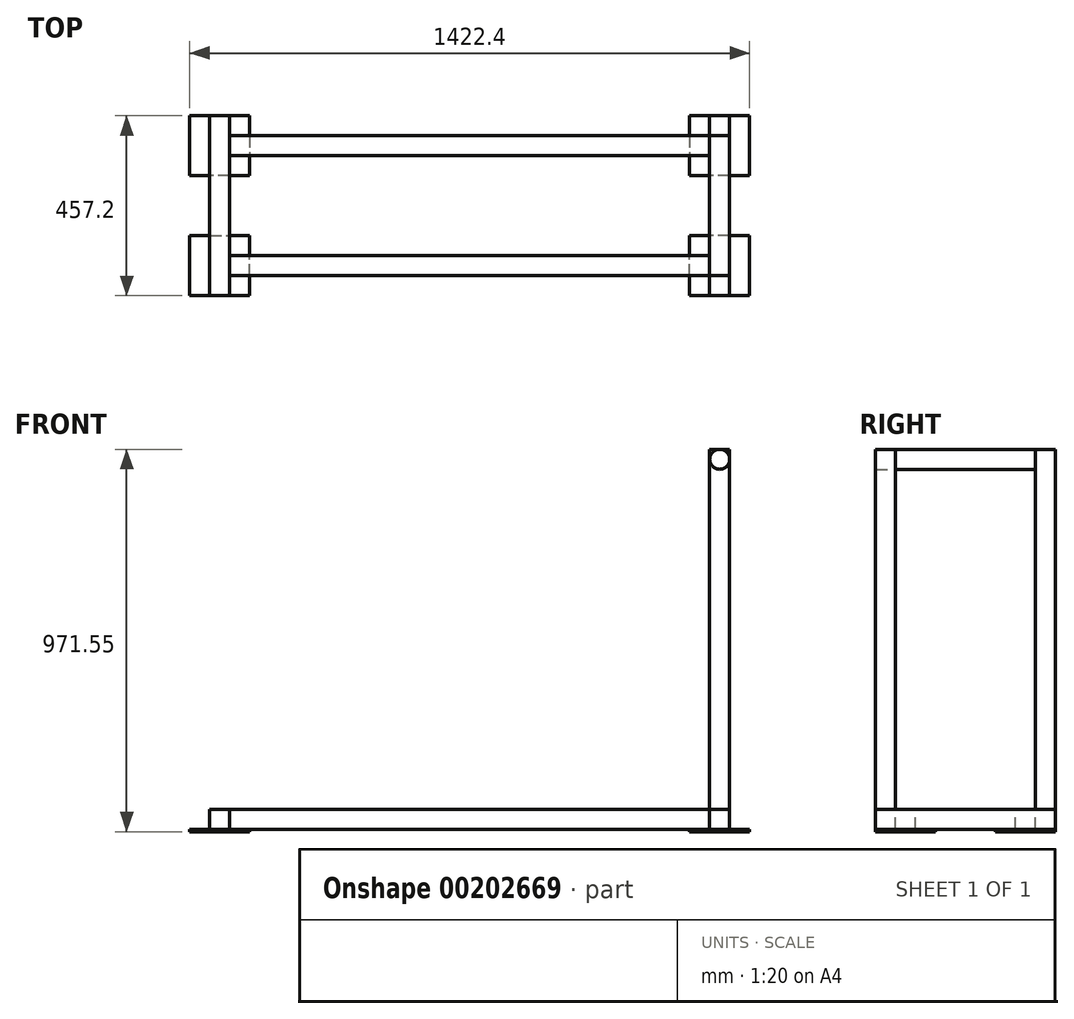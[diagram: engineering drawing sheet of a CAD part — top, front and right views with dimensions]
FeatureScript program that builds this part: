
annotation { "Feature Type Name" : "Feature", "Feature Type Description" : "" }
export const myFeature = defineFeature(function(context is Context, id is Id, definition is map)
    precondition{}
    {
        {
            var Q0;
            Q0=qCreatedBy(makeId("Right.planeOp"),FACE);
            var sketch = newSketch(context, id + "F0", { "sketchPlane" : qUnion([Q0])});
            skLineSegment(sketch, "E0.bottom", {"start": v(-228.6, 25.4) * mm, "end": v(228.6, 25.4) * mm});
            skLineSegment(sketch, "E0.top", {"start": v(-228.6, -25.4) * mm, "end": v(228.6, -25.4) * mm});
            skLineSegment(sketch, "E0.left", {"start": v(-228.6, 25.4) * mm, "end": v(-228.6, -25.4) * mm});
            skLineSegment(sketch, "E0.right", {"start": v(228.6, 25.4) * mm, "end": v(228.6, -25.4) * mm});
            skSolve(sketch);
        }
        {
            var Q0;
            Q0 = qSketchRegion(id + "F0", true);
            extrude(context, id + "F1", {"entities" : qUnion([Q0]), "endBound" : BoundingType.SYMMETRIC, "depth" : 50.8 * mm});
        }
        {
            var Q0;
            Q0=makeQuery(id+"F1.opExtrude","SWEPT_FACE",FACE,{"disambiguationData":[OSD([sQuery(id+"F0.wireOp",EDGE,"E0.bottom")])]});
            var sketch = newSketch(context, id + "F2", { "sketchPlane" : qUnion([Q0])});
            skLineSegment(sketch, "E1.bottom", {"start": v(-25.4, 177.8) * mm, "end": v(-1244.6, 177.8) * mm});
            skLineSegment(sketch, "E1.top", {"start": v(-25.4, 127) * mm, "end": v(-1244.6, 127) * mm});
            skLineSegment(sketch, "E1.left", {"start": v(-25.4, 177.8) * mm, "end": v(-25.4, 127) * mm});
            skLineSegment(sketch, "E1.right", {"start": v(-1244.6, 177.8) * mm, "end": v(-1244.6, 127) * mm});
            skLineSegment(sketch, "E2.bottom", {"start": v(-25.4, -177.8) * mm, "end": v(-1244.6, -177.8) * mm});
            skLineSegment(sketch, "E2.top", {"start": v(-25.4, -127) * mm, "end": v(-1244.6, -127) * mm});
            skLineSegment(sketch, "E2.left", {"start": v(-25.4, -177.8) * mm, "end": v(-25.4, -127) * mm});
            skLineSegment(sketch, "E2.right", {"start": v(-1244.6, -177.8) * mm, "end": v(-1244.6, -127) * mm});
            skSolve(sketch);
        }
        {
            var Q0;
            Q0 = qSketchRegion(id + "F2", true);
            extrude(context, id + "F3", {"entities" : qUnion([Q0]), "oppositeDirection" : true, "depth" : 50.8 * mm});
        }
        {
            var Q0;
            Q0=makeQuery(id+"F3.opExtrude","CAP_FACE",FACE,{"disambiguationData":[OSD([sQuery(id+"F2.wireOp",EDGE,"E1.bottom"),sQuery(id+"F2.wireOp",EDGE,"E1.top"),sQuery(id+"F2.wireOp",EDGE,"E1.left"),sQuery(id+"F2.wireOp",EDGE,"E1.right")])],"isStart":true});
            var sketch = newSketch(context, id + "F4", { "sketchPlane" : qUnion([Q0])});
            skLineSegment(sketch, "E3.bottom", {"start": v(-1244.6, 228.6) * mm, "end": v(-1295.4, 228.6) * mm});
            skLineSegment(sketch, "E3.top", {"start": v(-1244.6, -228.6) * mm, "end": v(-1295.4, -228.6) * mm});
            skLineSegment(sketch, "E3.left", {"start": v(-1244.6, 228.6) * mm, "end": v(-1244.6, -228.6) * mm});
            skLineSegment(sketch, "E3.right", {"start": v(-1295.4, 228.6) * mm, "end": v(-1295.4, -228.6) * mm});
            skSolve(sketch);
        }
        {
            var Q0;
            Q0 = qSketchRegion(id + "F4", true);
            extrude(context, id + "F5", {"entities" : qUnion([Q0]), "oppositeDirection" : true, "depth" : 50.8 * mm});
        }
        {
            var Q0;
            Q0=makeQuery(id+"F5.opExtrude","CAP_FACE",FACE,{"disambiguationData":[OSD([sQuery(id+"F4.wireOp",EDGE,"E3.bottom"),sQuery(id+"F4.wireOp",EDGE,"E3.top"),sQuery(id+"F4.wireOp",EDGE,"E3.left"),sQuery(id+"F4.wireOp",EDGE,"E3.right")])],"isStart":false});
            var sketch = newSketch(context, id + "F6", { "sketchPlane" : qUnion([Q0])});
            skLineSegment(sketch, "E4.bottom", {"start": v(-1346.2, 228.6) * mm, "end": v(-1193.8, 228.6) * mm});
            skLineSegment(sketch, "E4.top", {"start": v(-1346.2, 76.2) * mm, "end": v(-1193.8, 76.2) * mm});
            skLineSegment(sketch, "E4.left", {"start": v(-1346.2, 228.6) * mm, "end": v(-1346.2, 76.2) * mm});
            skLineSegment(sketch, "E4.right", {"start": v(-1193.8, 228.6) * mm, "end": v(-1193.8, 76.2) * mm});
            skLineSegment(sketch, "E5.bottom", {"start": v(-1193.8, -228.6) * mm, "end": v(-1346.2, -228.6) * mm});
            skLineSegment(sketch, "E5.top", {"start": v(-1193.8, -76.2) * mm, "end": v(-1346.2, -76.2) * mm});
            skLineSegment(sketch, "E5.left", {"start": v(-1193.8, -228.6) * mm, "end": v(-1193.8, -76.2) * mm});
            skLineSegment(sketch, "E5.right", {"start": v(-1346.2, -228.6) * mm, "end": v(-1346.2, -76.2) * mm});
            skLineSegment(sketch, "E6.bottom", {"start": v(76.2, 228.6) * mm, "end": v(-76.2, 228.6) * mm});
            skLineSegment(sketch, "E6.top", {"start": v(76.2, 76.2) * mm, "end": v(-76.2, 76.2) * mm});
            skLineSegment(sketch, "E6.left", {"start": v(76.2, 228.6) * mm, "end": v(76.2, 76.2) * mm});
            skLineSegment(sketch, "E6.right", {"start": v(-76.2, 228.6) * mm, "end": v(-76.2, 76.2) * mm});
            skLineSegment(sketch, "E7.bottom", {"start": v(76.2, -228.6) * mm, "end": v(-76.2, -228.6) * mm});
            skLineSegment(sketch, "E7.top", {"start": v(76.2, -76.2) * mm, "end": v(-76.2, -76.2) * mm});
            skLineSegment(sketch, "E7.left", {"start": v(76.2, -228.6) * mm, "end": v(76.2, -76.2) * mm});
            skLineSegment(sketch, "E7.right", {"start": v(-76.2, -228.6) * mm, "end": v(-76.2, -76.2) * mm});
            skSolve(sketch);
        }
        {
            var Q0;
            Q0 = qSketchRegion(id + "F6", true);
            extrude(context, id + "F7", {"entities" : qUnion([Q0]), "depth" : 6.35 * mm});
        }
        {
            var Q0;
            Q0=makeQuery(id+"F1.opExtrude","SWEPT_FACE",FACE,{"disambiguationData":[OSD([sQuery(id+"F0.wireOp",EDGE,"E0.bottom")])]});
            var sketch = newSketch(context, id + "F8", { "sketchPlane" : qUnion([Q0])});
            skLineSegment(sketch, "E8.bottom", {"start": v(-25.4, -228.6) * mm, "end": v(25.4, -228.6) * mm});
            skLineSegment(sketch, "E8.top", {"start": v(-25.4, -177.8) * mm, "end": v(25.4, -177.8) * mm});
            skLineSegment(sketch, "E8.left", {"start": v(-25.4, -228.6) * mm, "end": v(-25.4, -177.8) * mm});
            skLineSegment(sketch, "E8.right", {"start": v(25.4, -228.6) * mm, "end": v(25.4, -177.8) * mm});
            skLineSegment(sketch, "E9.bottom", {"start": v(-25.4, 228.6) * mm, "end": v(25.4, 228.6) * mm});
            skLineSegment(sketch, "E9.top", {"start": v(-25.4, 177.8) * mm, "end": v(25.4, 177.8) * mm});
            skLineSegment(sketch, "E9.left", {"start": v(-25.4, 228.6) * mm, "end": v(-25.4, 177.8) * mm});
            skLineSegment(sketch, "E9.right", {"start": v(25.4, 228.6) * mm, "end": v(25.4, 177.8) * mm});
            skSolve(sketch);
        }
        {
            var Q0;
            Q0 = qSketchRegion(id + "F8", true);
            extrude(context, id + "F9", {"entities" : qUnion([Q0]), "depth" : 914.4 * mm});
        }
        {
            var Q0;
            Q0=makeQuery(id+"F9.opExtrude","SWEPT_FACE",FACE,{"disambiguationData":[OSD([sQuery(id+"F8.wireOp",EDGE,"E9.top")])]});
            var sketch = newSketch(context, id + "F10", { "sketchPlane" : qUnion([Q0])});
            skCircle(sketch, "E10", {"center": v(0, 914.4) * mm, "radius": 25.4 * mm});
            skPoint(sketch, "E10.centerSnap0", {"position": v(0, 939.8) * mm});
            skSolve(sketch);
        }
        {
            var Q0;
            Q0 = qSketchRegion(id + "F10", true);
            extrude(context, id + "F11", {"entities" : qUnion([Q0]), "depth" : 406.4 * mm});
        }
    });
